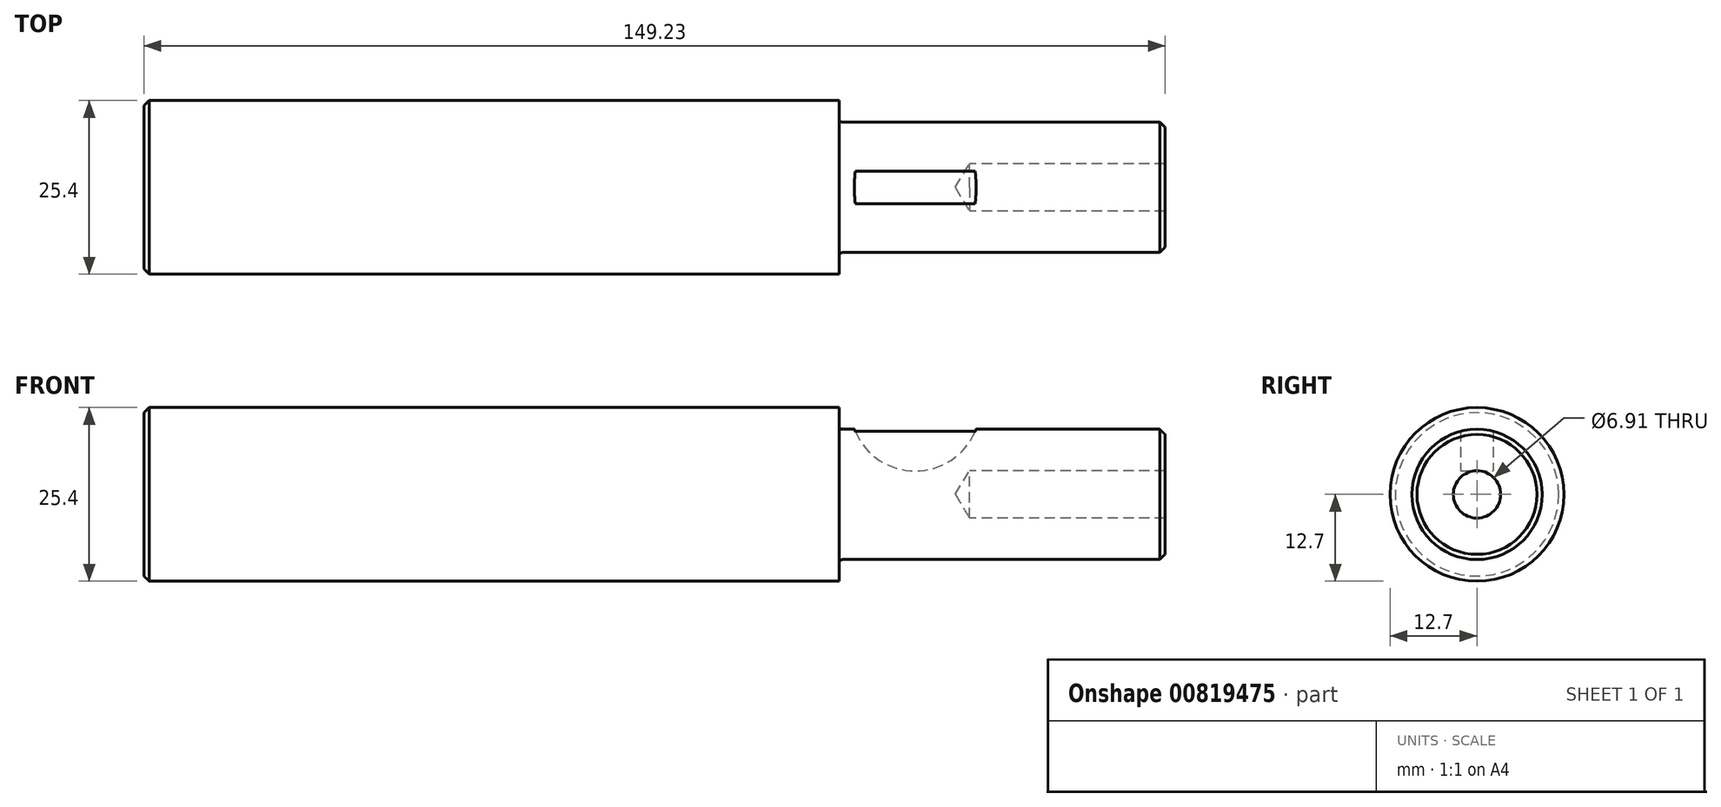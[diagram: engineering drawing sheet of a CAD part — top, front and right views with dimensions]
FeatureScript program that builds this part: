
annotation { "Feature Type Name" : "Feature", "Feature Type Description" : "" }
export const myFeature = defineFeature(function(context is Context, id is Id, definition is map)
    precondition{}
    {
        {
            var Q0;
            Q0=qCreatedBy(makeId("Front.planeOp"),FACE);
            var sketch = newSketch(context, id + "F0", { "sketchPlane" : qUnion([Q0])});
            skLineSegment(sketch, "E0", {"start": v(-101.6, 0) * mm, "end": v(47.63, 0) * mm});
            skLineSegment(sketch, "E1", {"start": v(47.63, 0) * mm, "end": v(47.63, 9.53) * mm});
            skLineSegment(sketch, "E2", {"start": v(47.63, 9.53) * mm, "end": v(0, 9.52) * mm});
            skLineSegment(sketch, "E3", {"start": v(0, 9.52) * mm, "end": v(0, 12.7) * mm});
            skLineSegment(sketch, "E4", {"start": v(0, 12.7) * mm, "end": v(-101.6, 12.7) * mm});
            skLineSegment(sketch, "E5", {"start": v(-101.6, 12.7) * mm, "end": v(-101.6, 0) * mm});
            skLineSegment(sketch, "E6.MirrorCS", {"start": v(-101.6, -12.7) * mm, "end": v(-101.6, 0) * mm});
            skLineSegment(sketch, "E7.MirrorCS", {"start": v(0, -12.7) * mm, "end": v(-101.6, -12.7) * mm});
            skLineSegment(sketch, "E8.MirrorCS", {"start": v(0, -9.52) * mm, "end": v(0, -12.7) * mm});
            skLineSegment(sketch, "E9.MirrorCS", {"start": v(47.63, -9.53) * mm, "end": v(0, -9.52) * mm});
            skLineSegment(sketch, "E10.MirrorCS", {"start": v(47.63, 0) * mm, "end": v(47.63, -9.53) * mm});
            skSolve(sketch);
        }
        {
            var Q0;
            Q0=makeQuery(id+"F0.imprint","IMPRINT",FACE,{"disambiguationData":[TD([[makeQuery(id+"F0.imprint","IMPRINT",EDGE,{"derivedFrom":sQuery(id+"F0.wireOp",EDGE,"E0")}),1.0]])]});
            var Q1;
            Q1=sQuery(id+"F0.wireOp",EDGE,"E0");
            revolve(context, id + "F1", {"surfaceOperationType" : NewSurfaceOperationType.NEW, "entities" : qUnion([Q0]), "axis" : qUnion([Q1]), "revolveType" : RevolveType.FULL});
        }
        {
            var Q0;
            Q0=makeQuery(id+"F1.opRevolve","SWEPT_FACE",FACE,{"disambiguationData":[OSD([sQuery(id+"F0.wireOp",EDGE,"E1")])]});
            var sketch = newSketch(context, id + "F2", { "sketchPlane" : qUnion([Q0])});
            skPoint(sketch, "E11", {"position": v(0, 0) * mm});
            skSolve(sketch);
        }
        {
            var Q0;
            Q0=sQuery(id+"F2.wireOp",VERTEX,"E11");
            var Q1;
            Q1=makeQuery(id+"F1.opRevolve","SWEPT_BODY",BODY,{"disambiguationData":[OSD([sQuery(id+"F0.wireOp",EDGE,"E0"),sQuery(id+"F0.wireOp",EDGE,"E1"),sQuery(id+"F0.wireOp",EDGE,"E2"),sQuery(id+"F0.wireOp",EDGE,"E3"),sQuery(id+"F0.wireOp",EDGE,"E4"),sQuery(id+"F0.wireOp",EDGE,"E5")])]});
            hole(context, id + "F3", {"style" : HoleStyle.SIMPLE, "endStyle" : HoleEndStyle.BLIND, "standardTappedOrClearance" : lookupTablePath({ "standard" : "ANSI", "engagement" : "75%", "pitch" : "24 tpi", "size" : "5/16", "type" : "Tapped" }), "standardBlindInLast" : lookupTablePath({ "standard" : "ANSI", "engagement" : "75%", "pitch" : "24 tpi", "size" : "5/16", "type" : "Tapped" }), "holeDiameter" : 6.9 * mm, "majorDiameter" : 7.94 * mm, "showTappedDepth" : true, "holeDepth" : 28.57 * mm, "tappedDepth" : 25.4 * mm, "tapClearance" : 3, "locations" : qUnion([Q0]), "scope" : qUnion([Q1]), "startStyle" : HoleStartStyle.SKETCH});
        }
        {
            var Q0;
            Q0=qCreatedBy(makeId("Front.planeOp"),FACE);
            var sketch = newSketch(context, id + "F4", { "sketchPlane" : qUnion([Q0])});
            skCircle(sketch, "E12", {"center": v(11.11, 12.95) * mm, "radius": 9.53 * mm});
            skLineSegment(sketch, "E13", {"start": v(0, 0) * mm, "end": v(53.06, 0) * mm, "construction": true});
            skSolve(sketch);
        }
        {
            var Q0;
            Q0=makeQuery(id+"F4.imprint","IMPRINT",FACE,{"disambiguationData":[TD([[makeQuery(id+"F4.imprint","IMPRINT",EDGE,{"derivedFrom":sQuery(id+"F4.wireOp",EDGE,"E12")}),1.0]])]});
            extrude(context, id + "F5", {"entities" : qUnion([Q0]), "operationType" : NewBodyOperationType.REMOVE, "depth" : 4.76 * mm, "offsetDistance" : 25.4 * mm, "symmetric" : true});
        }
        {
            var Q0;
            Q0=makeQuery(id+"F1.opRevolve","SWEPT_EDGE",EDGE,{"disambiguationData":[OSD([sQuery(id+"F0.wireOp",EDGE,"E2"),sQuery(id+"F0.wireOp",EDGE,"E3")])]});
            fillet(context, id + "F6", {"entities" : qUnion([Q0]), "tangentPropagation" : true, "radius" : 0.5 * mm, "defaultsChanged" : true, "vertexSettings" : [], "allowEdgeOverflow" : false});
        }
        {
            var Q0;
            Q0=makeQuery(id+"F1.opRevolve","SWEPT_EDGE",EDGE,{"disambiguationData":[OSD([sQuery(id+"F0.wireOp",EDGE,"E4"),sQuery(id+"F0.wireOp",EDGE,"E5")])]});
            var Q1;
            Q1=makeQuery(id+"F1.opRevolve","SWEPT_EDGE",EDGE,{"disambiguationData":[OSD([sQuery(id+"F0.wireOp",EDGE,"E1"),sQuery(id+"F0.wireOp",EDGE,"E2")])]});
            chamfer(context, id + "F7", {"entities" : qUnion([Q0, Q1]), "width" : 0.76 * mm, "tangentPropagation" : true});
        }
    });
